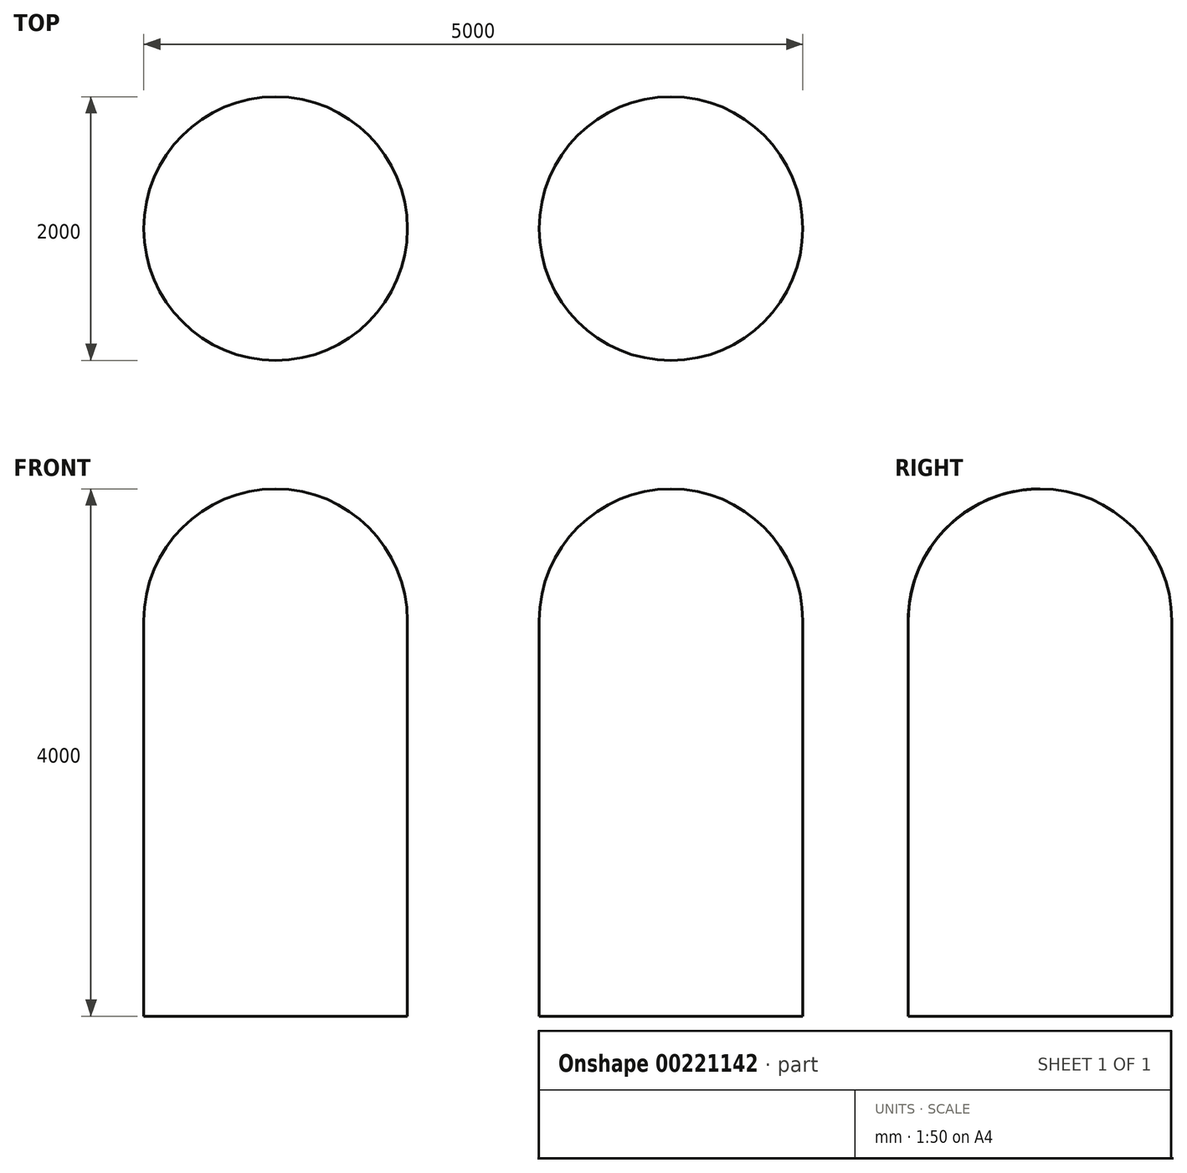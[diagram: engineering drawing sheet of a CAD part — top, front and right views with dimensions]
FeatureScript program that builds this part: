
annotation { "Feature Type Name" : "Feature", "Feature Type Description" : "" }
export const myFeature = defineFeature(function(context is Context, id is Id, definition is map)
    precondition{}
    {
        {
            var Q0;
            Q0=qCreatedBy(makeId("Right.planeOp"),FACE);
            var sketch = newSketch(context, id + "F0", { "sketchPlane" : qUnion([Q0])});
            skArc(sketch, "E0", {"start": v(0, 1000) * mm, "mid": v(-707.1, 707.1) * mm, "end": v(-1000, 0) * mm});
            skLineSegment(sketch, "E1", {"start": v(0, -3000) * mm, "end": v(-1000, -3000) * mm});
            skLineSegment(sketch, "E2", {"start": v(-1000, 0) * mm, "end": v(-1000, -3000) * mm});
            skLineSegment(sketch, "E3", {"start": v(0, -3000) * mm, "end": v(0, 1000) * mm});
            skSolve(sketch);
        }
        {
            var Q0;
            Q0=makeQuery(id+"F0.imprint","IMPRINT",FACE,{"disambiguationData":[TD([[makeQuery(id+"F0.imprint","IMPRINT",EDGE,{"derivedFrom":sQuery(id+"F0.wireOp",EDGE,"E0")}),1.0]])]});
            var Q1;
            Q1=sQuery(id+"F0.wireOp",EDGE,"E3");
            revolve(context, id + "F1", {"entities" : qUnion([Q0]), "axis" : qUnion([Q1]), "revolveType" : RevolveType.FULL});
        }
        {
            var Q0;
            Q0=makeQuery(id+"F1.opRevolve","SWEPT_BODY",BODY,{"disambiguationData":[OSD([sQuery(id+"F0.wireOp",EDGE,"E0"),sQuery(id+"F0.wireOp",EDGE,"E1"),sQuery(id+"F0.wireOp",EDGE,"E2"),sQuery(id+"F0.wireOp",EDGE,"E3")])]});
            transform(context, id + "F2", {"entities" : qUnion([Q0]), "transformType" : TransformType.TRANSLATION_3D, "dx" : 3000 * mm, "dy" : 0 * mm, "dz" : 0 * mm, "makeCopy" : true});
        }
    });
